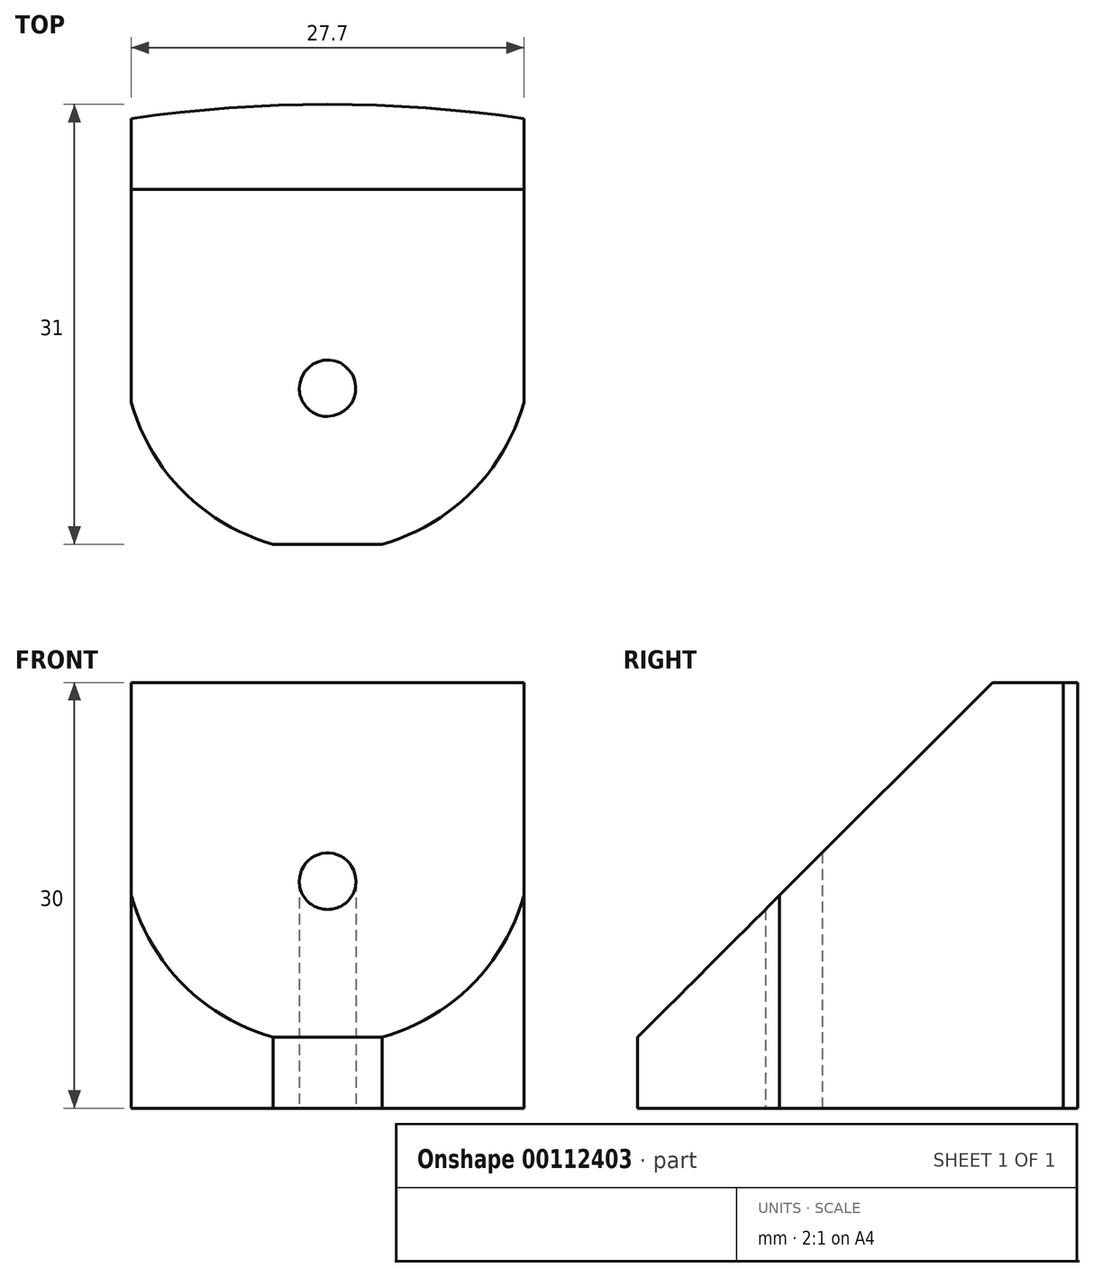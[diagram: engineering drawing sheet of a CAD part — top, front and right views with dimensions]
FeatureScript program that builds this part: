
annotation { "Feature Type Name" : "Feature", "Feature Type Description" : "" }
export const myFeature = defineFeature(function(context is Context, id is Id, definition is map)
    precondition{}
    {
        {
            var Q0;
            Q0=qCreatedBy(makeId("Top.planeOp"),FACE);
            var sketch = newSketch(context, id + "F0", { "sketchPlane" : qUnion([Q0])});
            skLineSegment(sketch, "E0.bottom", {"start": v(13.85, -15) * mm, "end": v(-13.85, -15) * mm});
            skLineSegment(sketch, "E0.top", {"start": v(13.85, 15) * mm, "end": v(-13.85, 15) * mm});
            skLineSegment(sketch, "E0.left", {"start": v(13.85, -15) * mm, "end": v(13.85, 15) * mm});
            skLineSegment(sketch, "E0.right", {"start": v(-13.85, -15) * mm, "end": v(-13.85, 15) * mm});
            skPoint(sketch, "E0.middle", {"position": v(0, 0) * mm});
            skLineSegment(sketch, "E1", {"start": v(0, 15) * mm, "end": v(0, 16) * mm, "construction": true});
            skArc(sketch, "E2", {"start": v(13.85, 15) * mm, "mid": v(0, 16) * mm, "end": v(-13.85, 15) * mm});
            skSolve(sketch);
        }
        {
            var Q0;
            Q0=makeQuery(id+"F0.imprint","IMPRINT",FACE,{"disambiguationData":[TD([[makeQuery(id+"F0.imprint","IMPRINT",EDGE,{"derivedFrom":sQuery(id+"F0.wireOp",EDGE,"E0.bottom")}),-1.0]])]});
            extrude(context, id + "F1", {"entities" : qUnion([Q0]), "depth" : 30 * mm});
        }
        {
            var Q0;
            Q0=makeQuery(id+"F1.opExtrude","SWEPT_FACE",FACE,{"disambiguationData":[OSD([sQuery(id+"F0.wireOp",EDGE,"E0.left")])]});
            var sketch = newSketch(context, id + "F2", { "sketchPlane" : qUnion([Q0])});
            skLineSegment(sketch, "E3", {"start": v(10, 30) * mm, "end": v(-15, 5) * mm});
            skLineSegment(sketch, "E4", {"start": v(-15, 5) * mm, "end": v(-15, 30) * mm});
            skLineSegment(sketch, "E5", {"start": v(-15, 30) * mm, "end": v(10, 30) * mm});
            skLineSegment(sketch, "E6", {"start": v(15, 30) * mm, "end": v(10, 30) * mm, "construction": true});
            skLineSegment(sketch, "E7", {"start": v(-15, 0) * mm, "end": v(-15, 5) * mm, "construction": true});
            skSolve(sketch);
        }
        {
            var Q0;
            Q0=makeQuery(id+"F1.opExtrude","CAP_FACE",FACE,{"disambiguationData":[OSD([sQuery(id+"F0.wireOp",EDGE,"E0.bottom"),sQuery(id+"F0.wireOp",EDGE,"E0.top"),sQuery(id+"F0.wireOp",EDGE,"E0.left"),sQuery(id+"F0.wireOp",EDGE,"E0.right")])],"isStart":false});
            var sketch = newSketch(context, id + "F3", { "sketchPlane" : qUnion([Q0])});
            skArc(sketch, "E8", {"start": v(13.85, 15) * mm, "mid": v(0, 16) * mm, "end": v(-13.85, 15) * mm});
            skLineSegment(sketch, "E9", {"start": v(-13.85, 15) * mm, "end": v(13.85, 15) * mm});
            skLineSegment(sketch, "E10", {"start": v(0, 15) * mm, "end": v(0.07, 16) * mm, "construction": true});
            skSolve(sketch);
        }
        {
            var Q1;
            Q1=makeQuery(id+"F0.imprint","IMPRINT",FACE,{"disambiguationData":[TD([[makeQuery(id+"F0.imprint","IMPRINT",EDGE,{"derivedFrom":sQuery(id+"F0.wireOp",EDGE,"E0.top")}),-1.0]])]});
            var Q2;
            Q2=makeQuery(id+"F3.imprint","IMPRINT",FACE,{"disambiguationData":[TD([[makeQuery(id+"F3.imprint","IMPRINT",EDGE,{"derivedFrom":sQuery(id+"F3.wireOp",EDGE,"E8")}),1.0]])]});
            loft(context, id + "F4", {"operationType" : NewBodyOperationType.ADD, "sheetProfilesArray" : [{ "sheetProfileEntities" : qUnion([Q1]) }, { "sheetProfileEntities" : qUnion([Q2]) }]});
        }
        {
            var Q0;
            Q0 = qSketchRegion(id + "F2", true);
            extrude(context, id + "F5", {"entities" : qUnion([Q0]), "operationType" : NewBodyOperationType.REMOVE, "endBound" : BoundingType.THROUGH_ALL, "oppositeDirection" : true, "depth" : 25 * mm});
        }
        {
            var Q0;
            Q0=makeQuery(id+"F1.opExtrude","CAP_FACE",FACE,{"disambiguationData":[OSD([sQuery(id+"F0.wireOp",EDGE,"E0.bottom"),sQuery(id+"F0.wireOp",EDGE,"E0.left"),sQuery(id+"F0.wireOp",EDGE,"E0.right"),sQuery(id+"F0.wireOp",EDGE,"WTfIm2Tz-BTHQ-jaCk-cCNo-Ye0gOjrFSvoi")])],"isStart":true});
            var sketch = newSketch(context, id + "F6", { "sketchPlane" : qUnion([Q0])});
            skLineSegment(sketch, "E11", {"start": v(0, -16) * mm, "end": v(0, 4) * mm, "construction": true});
            skCircle(sketch, "E12", {"center": v(0, 4) * mm, "radius": 2 * mm});
            skPoint(sketch, "E13.0", {"position": v(13.85, 15) * mm});
            skLineSegment(sketch, "E14", {"start": v(13.85, 15) * mm, "end": v(13.85, 5) * mm});
            skLineSegment(sketch, "E15", {"start": v(13.85, 15) * mm, "end": v(3.85, 15) * mm});
            skArc(sketch, "E16", {"start": v(13.85, 5) * mm, "mid": v(10.16, 11.31) * mm, "end": v(3.85, 15) * mm});
            skArc(sketch, "E17.MirrorCS", {"start": v(-13.85, 5) * mm, "mid": v(-10.16, 11.31) * mm, "end": v(-3.85, 15) * mm});
            skLineSegment(sketch, "E18.MirrorCS", {"start": v(-13.85, 15) * mm, "end": v(-13.85, 5) * mm});
            skLineSegment(sketch, "E19.MirrorCS", {"start": v(-13.85, 15) * mm, "end": v(-3.85, 15) * mm});
            skSolve(sketch);
        }
        {
            var Q0;
            Q0 = qSketchRegion(id + "F6", true);
            extrude(context, id + "F7", {"entities" : qUnion([Q0]), "operationType" : NewBodyOperationType.REMOVE, "endBound" : BoundingType.THROUGH_ALL, "oppositeDirection" : true, "depth" : 25 * mm});
        }
    });
